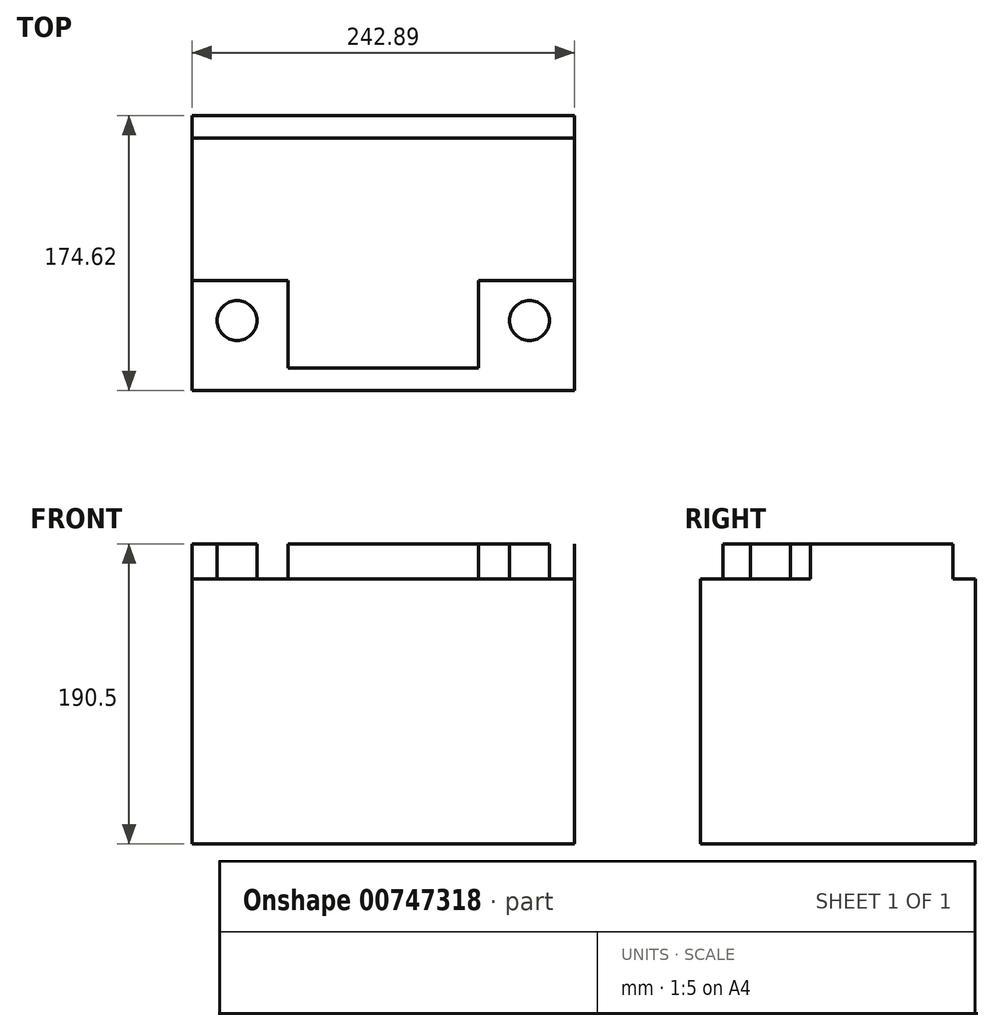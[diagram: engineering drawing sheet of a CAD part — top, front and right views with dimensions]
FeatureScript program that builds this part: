
annotation { "Feature Type Name" : "Feature", "Feature Type Description" : "" }
export const myFeature = defineFeature(function(context is Context, id is Id, definition is map)
    precondition{}
    {
        {
            var Q0;
            Q0=qCreatedBy(makeId("Top.planeOp"),FACE);
            var sketch = newSketch(context, id + "F0", { "sketchPlane" : qUnion([Q0])});
            skLineSegment(sketch, "E0.bottom", {"start": v(0, 0) * mm, "end": v(242.89, 0) * mm});
            skLineSegment(sketch, "E0.top", {"start": v(0, 174.63) * mm, "end": v(242.89, 174.63) * mm});
            skLineSegment(sketch, "E0.left", {"start": v(0, 0) * mm, "end": v(0, 174.63) * mm});
            skLineSegment(sketch, "E0.right", {"start": v(242.89, 0) * mm, "end": v(242.89, 174.63) * mm});
            skSolve(sketch);
        }
        {
            var Q0;
            Q0 = qSketchRegion(id + "F0", true);
            extrude(context, id + "F1", {"entities" : qUnion([Q0]), "depth" : 168.27 * mm, "offsetDistance" : 25.4 * mm});
        }
        {
            var Q0;
            Q0=makeQuery(id+"F1.opExtrude","CAP_FACE",FACE,{"disambiguationData":[OSD([sQuery(id+"F0.wireOp",EDGE,"E0.bottom"),sQuery(id+"F0.wireOp",EDGE,"E0.top"),sQuery(id+"F0.wireOp",EDGE,"E0.left"),sQuery(id+"F0.wireOp",EDGE,"E0.right")])],"isStart":false});
            var sketch = newSketch(context, id + "F2", { "sketchPlane" : qUnion([Q0])});
            skCircle(sketch, "E1", {"center": v(28.58, 44.45) * mm, "radius": 12.7 * mm});
            skCircle(sketch, "E2", {"center": v(214.31, 44.45) * mm, "radius": 12.7 * mm});
            skLineSegment(sketch, "E3", {"start": v(0, 160.34) * mm, "end": v(242.89, 160.34) * mm});
            skLineSegment(sketch, "E4", {"start": v(242.89, 160.34) * mm, "end": v(242.89, 69.85) * mm});
            skLineSegment(sketch, "E5", {"start": v(242.89, 69.85) * mm, "end": v(181.77, 69.85) * mm});
            skLineSegment(sketch, "E6", {"start": v(181.77, 69.85) * mm, "end": v(181.77, 14.29) * mm});
            skLineSegment(sketch, "E7", {"start": v(181.77, 14.29) * mm, "end": v(61.12, 14.29) * mm});
            skLineSegment(sketch, "E8", {"start": v(61.12, 14.29) * mm, "end": v(61.12, 69.85) * mm});
            skLineSegment(sketch, "E9", {"start": v(61.12, 69.85) * mm, "end": v(0, 69.85) * mm});
            skLineSegment(sketch, "E10", {"start": v(0, 69.85) * mm, "end": v(0, 160.34) * mm});
            skSolve(sketch);
        }
        {
            var Q0;
            Q0 = qSketchRegion(id + "F2", true);
            extrude(context, id + "F3", {"entities" : qUnion([Q0]), "operationType" : NewBodyOperationType.ADD, "depth" : 22.22 * mm, "offsetDistance" : 25.4 * mm});
        }
    });
